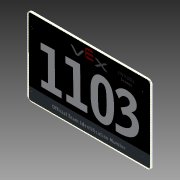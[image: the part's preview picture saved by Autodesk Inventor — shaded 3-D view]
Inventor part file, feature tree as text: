
AUTODESK INVENTOR PART (.ipt)
format: ipt  version: 2012 (Build 160160000, 160)  size: 355,328 bytes
history: native  units: in
note: dims shown in document units (in); Inventor stores cm internally (conversion verified against a paired STEP export)
features: sketch x2, extrude x1, fillet x1, plane x1, other x1
ambient origin geometry x8: Origin, YZ Plane, XZ Plane, XY Plane, X Axis, Y Axis, Z Axis, Center Point
feature tree (6):
  extrude  "Extrusion2"  Depth=2.125in
  fillet  "Fillet1"  Radius=0.182in
  plane  "Work Plane2"
  sketch  "Sketch12"  dims[d11=0.182in d12=0.182in d13=0.182in d16=0.0312in d17=0.0in d18=0.125in]
  sketch  "Sketch1"  dims[d0=3.375in d1=2.125in d10=0.182in]
  other  "Image3"
